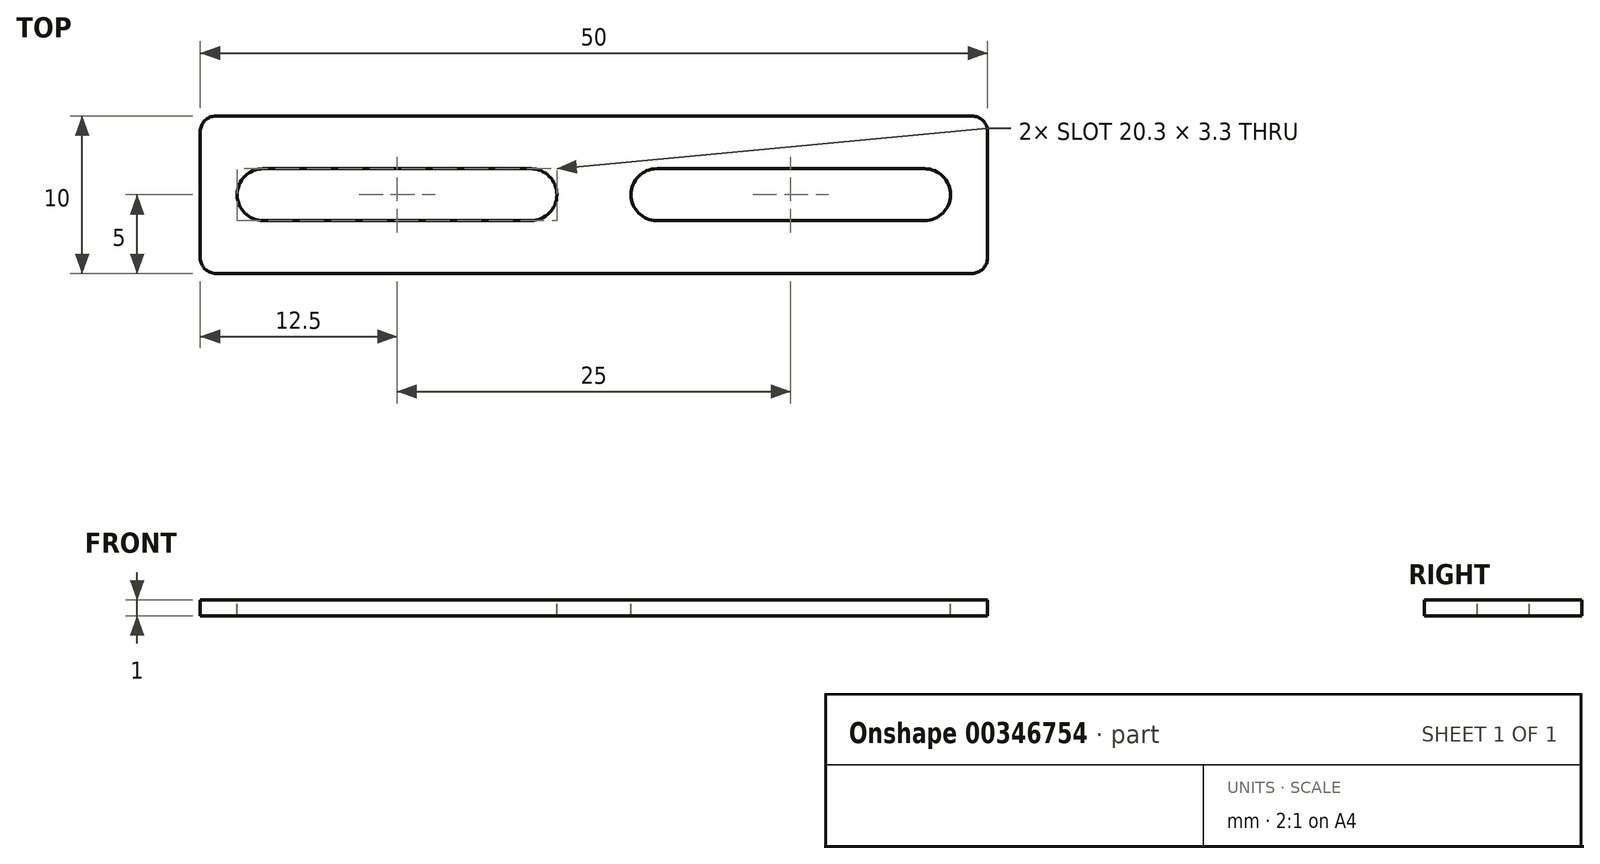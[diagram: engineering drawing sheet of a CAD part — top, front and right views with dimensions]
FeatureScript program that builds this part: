
annotation { "Feature Type Name" : "Feature", "Feature Type Description" : "" }
export const myFeature = defineFeature(function(context is Context, id is Id, definition is map)
    precondition{}
    {
        {
            var Q0;
            Q0=qCreatedBy(makeId("Top.planeOp"),FACE);
            var sketch = newSketch(context, id + "F0", { "sketchPlane" : qUnion([Q0])});
            skLineSegment(sketch, "E0.bottom", {"start": v(0, 10) * mm, "end": v(50, 10) * mm});
            skLineSegment(sketch, "E0.top", {"start": v(0, 0) * mm, "end": v(50, 0) * mm});
            skLineSegment(sketch, "E0.left", {"start": v(0, 10) * mm, "end": v(0, 0) * mm});
            skLineSegment(sketch, "E0.right", {"start": v(50, 10) * mm, "end": v(50, 0) * mm});
            skSolve(sketch);
        }
        {
            var Q0;
            Q0=makeQuery(id+"F0.imprint","IMPRINT",FACE,{"disambiguationData":[TD([[makeQuery(id+"F0.imprint","IMPRINT",EDGE,{"derivedFrom":sQuery(id+"F0.wireOp",EDGE,"E0.bottom")}),-1.0]])]});
            extrude(context, id + "F1", {"entities" : qUnion([Q0]), "depth" : 1 * mm});
        }
        {
            var Q0;
            Q0=makeQuery(id+"F1.opExtrude","CAP_FACE",FACE,{"disambiguationData":[OSD([sQuery(id+"F0.wireOp",EDGE,"E0.bottom"),sQuery(id+"F0.wireOp",EDGE,"E0.top"),sQuery(id+"F0.wireOp",EDGE,"E0.left"),sQuery(id+"F0.wireOp",EDGE,"E0.right")])],"isStart":false});
            var sketch = newSketch(context, id + "F2", { "sketchPlane" : qUnion([Q0])});
            skLineSegment(sketch, "E1", {"start": v(0, 5) * mm, "end": v(50, 5) * mm, "construction": true});
            skPoint(sketch, "E2", {"position": v(4, 5) * mm});
            skLineSegment(sketch, "E3", {"start": v(4, 10) * mm, "end": v(4, 0) * mm, "construction": true});
            skArc(sketch, "E4", {"start": v(4, 6.65) * mm, "mid": v(2.35, 5) * mm, "end": v(4, 3.35) * mm});
            skLineSegment(sketch, "E5", {"start": v(25, 10) * mm, "end": v(25, 0) * mm, "construction": true});
            skPoint(sketch, "E6", {"position": v(21, 5) * mm});
            skArc(sketch, "E7", {"start": v(21, 3.35) * mm, "mid": v(22.65, 5) * mm, "end": v(21, 6.65) * mm});
            skLineSegment(sketch, "E8", {"start": v(4, 6.65) * mm, "end": v(21, 6.65) * mm});
            skLineSegment(sketch, "E9", {"start": v(4, 3.35) * mm, "end": v(21, 3.35) * mm});
            skArc(sketch, "E10.MirrorCS", {"start": v(29, 3.35) * mm, "mid": v(27.35, 5) * mm, "end": v(29, 6.65) * mm});
            skLineSegment(sketch, "E11.MirrorCS", {"start": v(46, 3.35) * mm, "end": v(29, 3.35) * mm});
            skLineSegment(sketch, "E12.MirrorCS", {"start": v(46, 6.65) * mm, "end": v(29, 6.65) * mm});
            skArc(sketch, "E13.MirrorCS", {"start": v(46, 6.65) * mm, "mid": v(47.65, 5) * mm, "end": v(46, 3.35) * mm});
            skSolve(sketch);
        }
        {
            var Q0;
            Q0 = qSketchRegion(id + "F2", true);
            extrude(context, id + "F3", {"entities" : qUnion([Q0]), "operationType" : NewBodyOperationType.REMOVE, "oppositeDirection" : true, "depth" : 25 * mm});
        }
        {
            var Q0;
            Q0=makeQuery(id+"F1.opExtrude","SWEPT_EDGE",EDGE,{"disambiguationData":[OSD([sQuery(id+"F0.wireOp",EDGE,"E0.top"),sQuery(id+"F0.wireOp",EDGE,"E0.right")])]});
            var Q1;
            Q1=makeQuery(id+"F1.opExtrude","SWEPT_EDGE",EDGE,{"disambiguationData":[OSD([sQuery(id+"F0.wireOp",EDGE,"E0.bottom"),sQuery(id+"F0.wireOp",EDGE,"E0.right")])]});
            var Q2;
            Q2=makeQuery(id+"F1.opExtrude","SWEPT_EDGE",EDGE,{"disambiguationData":[OSD([sQuery(id+"F0.wireOp",EDGE,"E0.bottom"),sQuery(id+"F0.wireOp",EDGE,"E0.left")])]});
            var Q3;
            Q3=makeQuery(id+"F1.opExtrude","SWEPT_EDGE",EDGE,{"disambiguationData":[OSD([sQuery(id+"F0.wireOp",EDGE,"E0.top"),sQuery(id+"F0.wireOp",EDGE,"E0.left")])]});
            fillet(context, id + "F4", {"entities" : qUnion([Q0, Q1, Q2, Q3]), "radius" : 1 * mm, "tangentPropagation" : true, "allowEdgeOverflow" : false});
        }
    });
